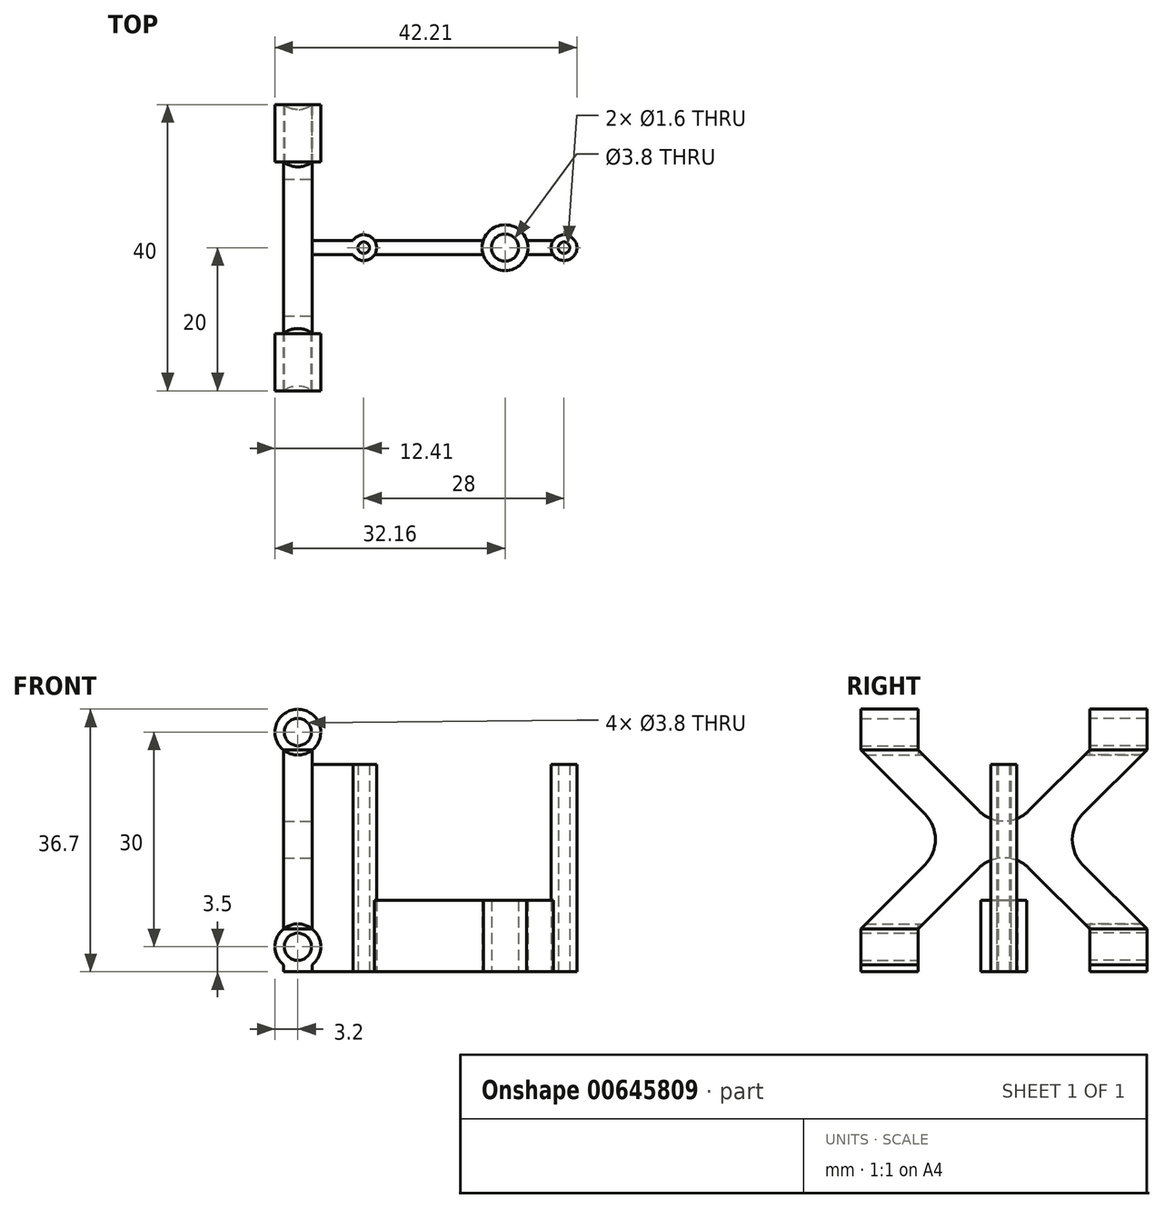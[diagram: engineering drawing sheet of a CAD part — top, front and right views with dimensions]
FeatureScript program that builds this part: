
annotation { "Feature Type Name" : "Feature", "Feature Type Description" : "" }
export const myFeature = defineFeature(function(context is Context, id is Id, definition is map)
    precondition{}
    {
        {
            var Q0;
            Q0=qCreatedBy(makeId("Top.planeOp"),FACE);
            var sketch = newSketch(context, id + "F0", { "sketchPlane" : qUnion([Q0])});
            skCircle(sketch, "E0", {"center": v(0, 0) * mm, "radius": 3.2 * mm});
            skCircle(sketch, "E1", {"center": v(0, 0) * mm, "radius": 1.9 * mm});
            skCircle(sketch, "E2", {"center": v(8.25, 0) * mm, "radius": 0.8 * mm});
            skCircle(sketch, "E3", {"center": v(8.25, 0) * mm, "radius": 1.8 * mm});
            skCircle(sketch, "E4", {"center": v(-19.75, 0) * mm, "radius": 0.8 * mm});
            skCircle(sketch, "E5", {"center": v(-19.75, 0) * mm, "radius": 1.8 * mm});
            skLineSegment(sketch, "E6", {"start": v(-26.96, 1) * mm, "end": v(-21.25, 1) * mm});
            skLineSegment(sketch, "E7", {"start": v(-26.96, -1) * mm, "end": v(-21.25, -1) * mm});
            skLineSegment(sketch, "E8", {"start": v(-18.25, 1) * mm, "end": v(-3.04, 1) * mm});
            skLineSegment(sketch, "E9", {"start": v(-18.25, -1) * mm, "end": v(-3.04, -1) * mm});
            skLineSegment(sketch, "E10", {"start": v(3.04, 1) * mm, "end": v(6.75, 1) * mm});
            skLineSegment(sketch, "E11", {"start": v(3.04, -1) * mm, "end": v(6.75, -1) * mm});
            skLineSegment(sketch, "E12", {"start": v(-26.96, 1) * mm, "end": v(-26.96, -1) * mm});
            skSolve(sketch);
        }
        {
            var Q0;
            Q0=makeQuery(id+"F0.imprint","IMPRINT",FACE,{"disambiguationData":[TD([[makeQuery(id+"F0.imprint","IMPRINT",EDGE,{"derivedFrom":sQuery(id+"F0.wireOp",EDGE,"E4")}),-1.0]])]});
            var Q1;
            Q1=makeQuery(id+"F0.imprint","IMPRINT",FACE,{"disambiguationData":[TD([[makeQuery(id+"F0.imprint","IMPRINT",EDGE,{"derivedFrom":sQuery(id+"F0.wireOp",EDGE,"E2")}),-1.0]])]});
            var Q2;
            {var subQ0=sQuery(id+"F0.wireOp",EDGE,"E6");Q2=makeQuery(id+"F0.imprint","IMPRINT",FACE,{"disambiguationData":[TD([[makeQuery(id+"F0.imprint","IMPRINT",EDGE,{"derivedFrom":subQ0}),-1.0]])]});}
            extrude(context, id + "F1", {"entities" : qUnion([Q0, Q1, Q2]), "depth" : 29 * mm, "offsetDistance" : 25 * mm});
        }
        {
            var Q0;
            {var subQ0=sQuery(id+"F0.wireOp",EDGE,"E8");Q0=makeQuery(id+"F0.imprint","IMPRINT",FACE,{"disambiguationData":[TD([[makeQuery(id+"F0.imprint","IMPRINT",EDGE,{"derivedFrom":subQ0}),-1.0]])]});}
            var Q1;
            {var subQ0=sQuery(id+"F0.wireOp",EDGE,"E10");Q1=makeQuery(id+"F0.imprint","IMPRINT",FACE,{"disambiguationData":[TD([[makeQuery(id+"F0.imprint","IMPRINT",EDGE,{"derivedFrom":subQ0}),-1.0]])]});}
            extrude(context, id + "F2", {"entities" : qUnion([Q0, Q1]), "depth" : 10 * mm, "offsetDistance" : 25 * mm});
        }
        {
            var Q0;
            Q0=makeQuery(id+"F0.imprint","IMPRINT",FACE,{"disambiguationData":[TD([[makeQuery(id+"F0.imprint","IMPRINT",EDGE,{"derivedFrom":sQuery(id+"F0.wireOp",EDGE,"E1")}),-1.0]])]});
            extrude(context, id + "F3", {"entities" : qUnion([Q0]), "depth" : 10 * mm, "offsetDistance" : 25 * mm});
        }
        {
            var Q0;
            Q0=qCreatedBy(makeId("Front.planeOp"),FACE);
            var sketch = newSketch(context, id + "F4", { "sketchPlane" : qUnion([Q0])});
            skCircle(sketch, "E13", {"center": v(-28.96, 3.5) * mm, "radius": 1.9 * mm});
            skCircle(sketch, "E14", {"center": v(-28.96, 33.5) * mm, "radius": 1.9 * mm});
            skCircle(sketch, "E15", {"center": v(-28.96, 33.5) * mm, "radius": 3.2 * mm});
            skCircle(sketch, "E16", {"center": v(-28.96, 3.5) * mm, "radius": 3.2 * mm});
            skLineSegment(sketch, "E17", {"start": v(-28.96, 33.5) * mm, "end": v(-28.96, 3.5) * mm, "construction": true});
            skLineSegment(sketch, "E18", {"start": v(-30.96, 1) * mm, "end": v(-30.96, 0) * mm});
            skLineSegment(sketch, "E19", {"start": v(-30.96, 0) * mm, "end": v(-26.96, 0) * mm});
            skLineSegment(sketch, "E20", {"start": v(-26.96, 0) * mm, "end": v(-26.96, 1) * mm});
            skLineSegment(sketch, "E21", {"start": v(0, 0) * mm, "end": v(-47.25, 0) * mm, "construction": true});
            skLineSegment(sketch, "E22", {"start": v(-30.96, 6) * mm, "end": v(-30.96, 31) * mm});
            skLineSegment(sketch, "E23", {"start": v(-26.96, 31) * mm, "end": v(-26.96, 6) * mm});
            skSolve(sketch);
        }
        {
            var Q0;
            Q0=makeQuery(id+"F4.imprint","IMPRINT",FACE,{"disambiguationData":[TD([[makeQuery(id+"F4.imprint","IMPRINT",EDGE,{"derivedFrom":sQuery(id+"F4.wireOp",EDGE,"E14")}),-1.0]])]});
            var Q1;
            Q1=makeQuery(id+"F4.imprint","IMPRINT",FACE,{"disambiguationData":[TD([[makeQuery(id+"F4.imprint","IMPRINT",EDGE,{"derivedFrom":sQuery(id+"F4.wireOp",EDGE,"E13")}),-1.0]])]});
            var Q2;
            {var subQ0=sQuery(id+"F4.wireOp",EDGE,"E18");Q2=makeQuery(id+"F4.imprint","IMPRINT",FACE,{"disambiguationData":[TD([[makeQuery(id+"F4.imprint","IMPRINT",EDGE,{"derivedFrom":subQ0}),1.0]])]});}
            extrude(context, id + "F5", {"entities" : qUnion([Q0, Q1, Q2]), "depth" : 20 * mm, "offsetDistance" : 25 * mm, "hasSecondDirection" : true, "secondDirectionOppositeDirection" : false, "secondDirectionDepth" : 12 * mm});
        }
        {
            var Q0;
            Q0=makeQuery(id+"F4.imprint","IMPRINT",FACE,{"disambiguationData":[TD([[makeQuery(id+"F4.imprint","IMPRINT",EDGE,{"derivedFrom":sQuery(id+"F4.wireOp",EDGE,"E14")}),-1.0]])]});
            var Q1;
            Q1=makeQuery(id+"F4.imprint","IMPRINT",FACE,{"disambiguationData":[TD([[makeQuery(id+"F4.imprint","IMPRINT",EDGE,{"derivedFrom":sQuery(id+"F4.wireOp",EDGE,"E13")}),-1.0]])]});
            var Q2;
            {var subQ0=sQuery(id+"F4.wireOp",EDGE,"E18");Q2=makeQuery(id+"F4.imprint","IMPRINT",FACE,{"disambiguationData":[TD([[makeQuery(id+"F4.imprint","IMPRINT",EDGE,{"derivedFrom":subQ0}),1.0]])]});}
            extrude(context, id + "F6", {"entities" : qUnion([Q0, Q1, Q2]), "depth" : -20 * mm, "offsetDistance" : 25 * mm, "hasSecondDirection" : true, "secondDirectionOppositeDirection" : true, "secondDirectionDepth" : 12 * mm});
        }
        {
            var Q0;
            {var subQ0=sQuery(id+"F4.wireOp",EDGE,"E22");Q0=makeQuery(id+"F4.imprint","IMPRINT",FACE,{"disambiguationData":[TD([[makeQuery(id+"F4.imprint","IMPRINT",EDGE,{"derivedFrom":subQ0}),-1.0]])]});}
            extrude(context, id + "F7", {"entities" : qUnion([Q0]), "endBound" : BoundingType.SYMMETRIC, "depth" : 40 * mm, "offsetDistance" : 25 * mm});
        }
        {
            var Q0;
            Q0=makeQuery(id+"F7.opExtrude","SWEPT_FACE",FACE,{"disambiguationData":[OSD([sQuery(id+"F4.wireOp",EDGE,"E22")])]});
            var sketch = newSketch(context, id + "F8", { "sketchPlane" : qUnion([Q0])});
            skLineSegment(sketch, "E24", {"start": v(-12, 31) * mm, "end": v(0, 19) * mm});
            skLineSegment(sketch, "E25", {"start": v(0, 19) * mm, "end": v(12, 31) * mm});
            skLineSegment(sketch, "E26", {"start": v(-12, 6) * mm, "end": v(0, 18) * mm});
            skLineSegment(sketch, "E27", {"start": v(0, 18) * mm, "end": v(12, 6) * mm});
            skLineSegment(sketch, "E28", {"start": v(-20, 31) * mm, "end": v(-7.5, 18.5) * mm});
            skLineSegment(sketch, "E29", {"start": v(-7.5, 18.5) * mm, "end": v(-20, 6) * mm});
            skLineSegment(sketch, "E30", {"start": v(20, 31) * mm, "end": v(7.5, 18.5) * mm});
            skLineSegment(sketch, "E31", {"start": v(7.5, 18.5) * mm, "end": v(20, 6) * mm});
            skSolve(sketch);
        }
        {
            var Q0;
            Q0=makeQuery(id+"F8.imprint","IMPRINT",FACE,{"disambiguationData":[TD([[makeQuery(id+"F8.imprint","IMPRINT",EDGE,{"derivedFrom":sQuery(id+"F8.wireOp",EDGE,"E28")}),-1.0]])]});
            var Q1;
            {var subQ0=sQuery(id+"F8.wireOp",EDGE,"E24");Q1=makeQuery(id+"F8.imprint","IMPRINT",FACE,{"disambiguationData":[TD([[makeQuery(id+"F8.imprint","IMPRINT",EDGE,{"derivedFrom":subQ0}),1.0]])]});}
            var Q2;
            Q2=makeQuery(id+"F8.imprint","IMPRINT",FACE,{"disambiguationData":[TD([[makeQuery(id+"F8.imprint","IMPRINT",EDGE,{"derivedFrom":sQuery(id+"F8.wireOp",EDGE,"E30")}),1.0]])]});
            var Q3;
            {var subQ0=sQuery(id+"F8.wireOp",EDGE,"E26");Q3=makeQuery(id+"F8.imprint","IMPRINT",FACE,{"disambiguationData":[TD([[makeQuery(id+"F8.imprint","IMPRINT",EDGE,{"derivedFrom":subQ0}),-1.0]])]});}
            extrude(context, id + "F9", {"entities" : qUnion([Q0, Q1, Q2, Q3]), "operationType" : NewBodyOperationType.REMOVE, "endBound" : BoundingType.UP_TO_NEXT, "oppositeDirection" : true, "depth" : 25 * mm, "offsetDistance" : 25 * mm});
        }
        {
            var Q0;
            Q0=makeQuery(id+"F9.boolean.opBoolean","COPY",EDGE,{"derivedFrom":makeQuery(id+"F9.opExtrude","SWEPT_EDGE",EDGE,{"disambiguationData":[OSD([sQuery(id+"F8.wireOp",EDGE,"E28"),sQuery(id+"F8.wireOp",EDGE,"E29")])]})});
            var Q1;
            Q1=makeQuery(id+"F9.boolean.opBoolean","COPY",EDGE,{"derivedFrom":makeQuery(id+"F9.opExtrude","SWEPT_EDGE",EDGE,{"disambiguationData":[OSD([sQuery(id+"F8.wireOp",EDGE,"E30"),sQuery(id+"F8.wireOp",EDGE,"E31")])]})});
            var Q2;
            Q2=makeQuery(id+"F9.boolean.opBoolean","COPY",EDGE,{"derivedFrom":makeQuery(id+"F9.opExtrude","SWEPT_EDGE",EDGE,{"disambiguationData":[OSD([sQuery(id+"F8.wireOp",EDGE,"E24"),sQuery(id+"F8.wireOp",EDGE,"E25")])]})});
            var Q3;
            Q3=makeQuery(id+"F9.boolean.opBoolean","COPY",EDGE,{"derivedFrom":makeQuery(id+"F9.opExtrude","SWEPT_EDGE",EDGE,{"disambiguationData":[OSD([sQuery(id+"F8.wireOp",EDGE,"E26"),sQuery(id+"F8.wireOp",EDGE,"E27")])]})});
            fillet(context, id + "F10", {"entities" : qUnion([Q0, Q1, Q2, Q3]), "radius" : 5 * mm, "tangentPropagation" : true, "allowEdgeOverflow" : false});
        }
    });
